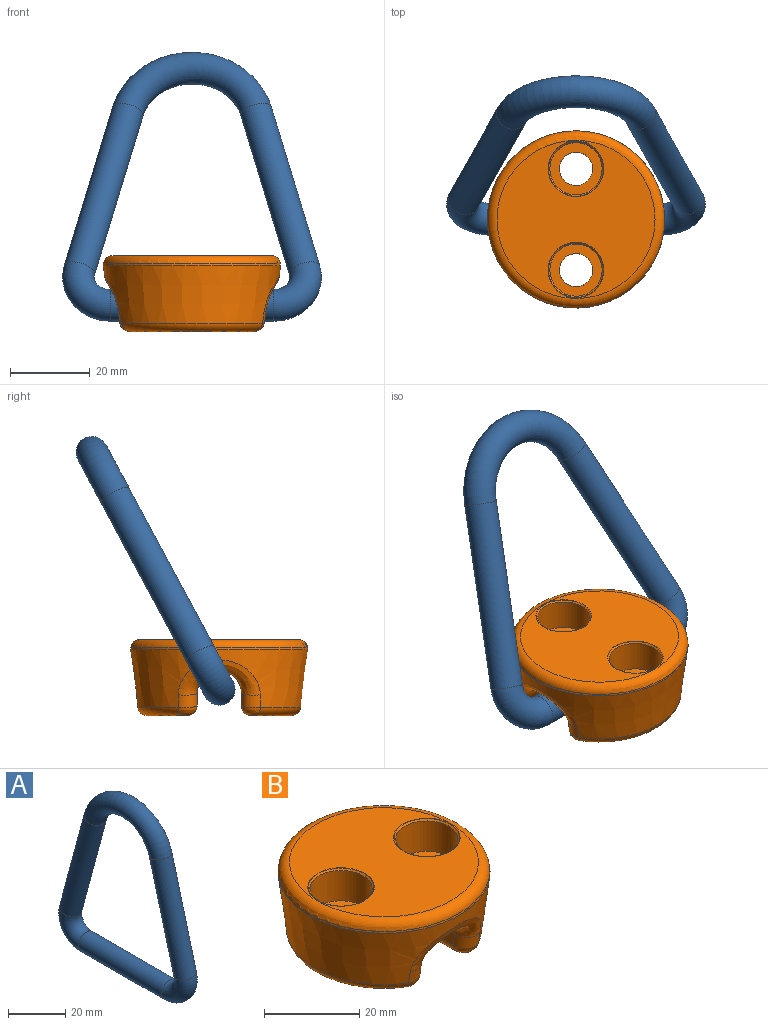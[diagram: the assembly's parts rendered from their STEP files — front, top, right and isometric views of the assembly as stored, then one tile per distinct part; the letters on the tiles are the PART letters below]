
ASSEMBLY  parts=2 mates=1
PART A: 6 faces, bbox 7.9x66.8x78.1 mm
  f0: cylinder r=3.97mm len=47.18mm, axis (0,0.26,0.97), area 1164.9mm2, adj f1,f5
  f1: torus R=7.94mm, axis (-1,0,0), area 362.7mm2, adj f0,f2
  f2: cylinder r=3.97mm len=41.05mm, axis (0,-1,0), area 1023.6mm2, adj f1,f3
  f3: torus R=7.94mm, axis (-1,0,0), area 362.7mm2, adj f2,f4
  f4: cylinder r=3.97mm len=47.18mm, axis (0,0.26,-0.97), area 1164.9mm2, adj f3,f5
  f5: torus R=16.67mm, axis (1,0,0), area 1088.2mm2, adj f0,f4
PART B: 44 faces, bbox 48x48x32 mm
  f0: plane 39.61x39.61mm, normal (0,0,1), area 926.8mm2, adj f22,f42,f43
  f1: cylinder r=5.56mm len=30.74mm, axis (0,1,0), area 274.6mm2, adj f6,f7,f9,f12,f32,f33,f34,f35
  f2: plane 31.44x10.14mm, normal (0,0,-1), area 170mm2, adj f14,f15,f16,f17,f39
  f3: cone r=22.23mm half-angle=7deg, axis (0,0,-1), area 63.1mm2, adj f4,f22
  f4: cone r=22.23mm half-angle=7deg, axis (0,0,1), area 1520.3mm2, adj f3,f8,f9,f10,f11,f12,f13,f16
  f5: plane 31.44x10.14mm, normal (0,0,-1), area 170mm2, adj f18,f19,f20,f21,f38
  f6: plane 30.74x3.18mm, normal (1,0,0), area 96.2mm2, adj f1,f8,f13,f15
  f7: plane 30.74x3.18mm, normal (-1,0,0), area 96.2mm2, adj f1,f10,f11,f20
  f8: bspline ~26.1x8.53mm, area 21mm2, adj f4,f6,f9,f17
  f9: bspline ~20.6x10.49mm, area 128mm2, adj f1,f4,f8,f10
  f10: bspline ~32.03x9.37mm, area 20.9mm2, adj f4,f7,f9,f21
  f11: bspline ~26.1x8.53mm, area 21mm2, adj f4,f7,f12,f18
  f12: bspline ~20.6x10.49mm, area 128mm2, adj f1,f4,f11,f13
  f13: bspline ~32.03x9.37mm, area 20.9mm2, adj f4,f6,f12,f14
  f14: bspline ~5.36x3.34mm, area 16.6mm2, adj f2,f13,f15,f16
  f15: cylinder r=2.39mm len=29.84mm, axis (0,-1,0), area 111.9mm2, adj f2,f6,f14,f17
  f16: torus R=18.09mm, axis (0,0,-1), area 140.7mm2, adj f2,f4,f14,f17
  f17: bspline ~5.37x3.89mm, area 16.6mm2, adj f2,f8,f15,f16
  f18: bspline ~5.37x3.89mm, area 16.6mm2, adj f5,f11,f19,f20
  f19: torus R=18.09mm, axis (0,0,-1), area 140.7mm2, adj f4,f5,f18,f21
  f20: cylinder r=2.39mm len=29.84mm, axis (0,1,0), area 111.9mm2, adj f5,f7,f18,f21
  f21: bspline ~5.36x3.34mm, area 16.6mm2, adj f5,f10,f19,f20
  f22: torus R=19.81mm, axis (0,0,1), area 460.6mm2, adj f0,f3
  f23: cylinder r=6.54mm len=13.08mm, axis (0,0,1), area 320.5mm2, adj f24,f41
  f24: plane 13.08x13.08mm, normal (0,0,1), area 79.9mm2, adj f23,f25
  f25: cylinder r=4.17mm len=10.49mm, axis (0,0,1), area 274.6mm2, adj f24,f38
  f26: cylinder r=6.54mm len=13.08mm, axis (0,0,1), area 320.5mm2, adj f27,f40
  f27: plane 13.08x13.08mm, normal (0,0,1), area 79.9mm2, adj f26,f28
  f28: cylinder r=4.17mm len=10.49mm, axis (0,0,1), area 274.6mm2, adj f27,f39
  f29: cylinder r=5.56mm len=14.86mm, axis (0,-1,0), area 273.5mm2, adj f30,f31,f32,f37
  f30: torus R=5.05mm, axis (0,-1,0), area 7.2mm2, adj f29,f34,f36
  f31: torus R=5.05mm, axis (0,-1,0), area 7.2mm2, adj f29,f33,f35
  f32: cylinder r=0.51mm len=14.86mm, axis (0,1,0), area 1.3mm2, adj f1,f29,f33,f34
  f33: bspline ~5.89x5.61mm, area 5mm2, adj f1,f31,f32,f35
  f34: bspline ~6.89x5.61mm, area 5mm2, adj f1,f30,f32,f36
  f35: bspline ~6.89x5.61mm, area 5mm2, adj f1,f31,f33,f37
  f36: bspline ~6.89x5.61mm, area 5mm2, adj f1,f30,f34,f37
  f37: cylinder r=0.51mm len=14.86mm, axis (0,-1,0), area 1.3mm2, adj f1,f29,f35,f36
  f38: cone r=4.55mm half-angle=45deg, axis (0,0,-1), area 14.7mm2, adj f5,f25
  f39: cone r=4.55mm half-angle=45deg, axis (0,0,-1), area 14.7mm2, adj f2,f28
  f40: cone r=6.54mm half-angle=45deg, axis (0,0,1), area 20.5mm2, adj f26,f43
  f41: cone r=6.54mm half-angle=45deg, axis (0,0,1), area 20.5mm2, adj f23,f42
  f42: torus R=6.97mm, axis (0,0,1), area 4.3mm2, adj f0,f41
  f43: torus R=6.97mm, axis (0,0,1), area 4.3mm2, adj f0,f40
PLACE A rot(axis=(-0.24,-0.24,-0.94),93.4deg) t=(0,31.93,66.02)mm
PLACE B rot(axis=(0,0,1),90deg) t=(0,0,16.51)mm fixed
MATE revolute A.f2 <-> B.f29  axis (-1,0,0) through (0,0,6.58)mm
